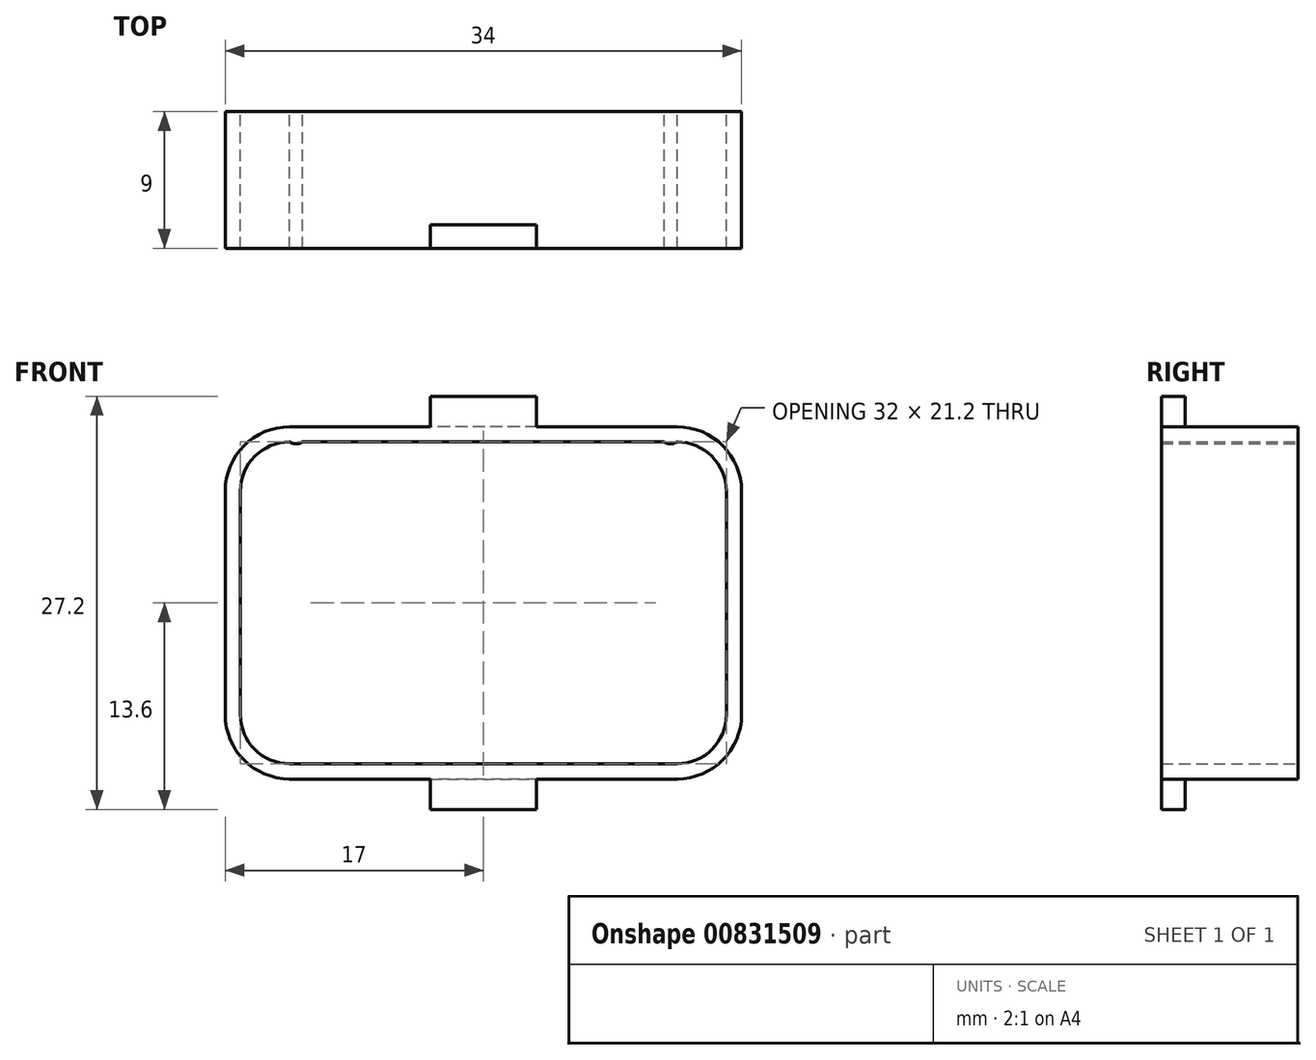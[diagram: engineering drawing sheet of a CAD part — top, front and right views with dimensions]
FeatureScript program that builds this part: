
annotation { "Feature Type Name" : "Feature", "Feature Type Description" : "" }
export const myFeature = defineFeature(function(context is Context, id is Id, definition is map)
    precondition{}
    {
        {
            var Q0;
            Q0=qCreatedBy(makeId("Front.planeOp"),FACE);
            var sketch = newSketch(context, id + "F0", { "sketchPlane" : qUnion([Q0])});
            skLineSegment(sketch, "E0.bottom", {"start": v(12.75, -10.6) * mm, "end": v(-12.75, -10.6) * mm});
            skLineSegment(sketch, "E0.top", {"start": v(12.75, 10.6) * mm, "end": v(-12.75, 10.6) * mm});
            skLineSegment(sketch, "E0.left", {"start": v(16, -7.35) * mm, "end": v(16, 7.35) * mm});
            skLineSegment(sketch, "E0.right", {"start": v(-16, -7.35) * mm, "end": v(-16, 7.35) * mm});
            skPoint(sketch, "E0.middle", {"position": v(0, 0) * mm});
            skPoint(sketch, "E1.visualSharp", {"position": v(-16, 10.6) * mm});
            skArc(sketch, "E1.filletArc", {"start": v(-12.75, 10.6) * mm, "mid": v(-15.05, 9.65) * mm, "end": v(-16, 7.35) * mm});
            skPoint(sketch, "E2.visualSharp", {"position": v(-16, -10.6) * mm});
            skArc(sketch, "E2.filletArc", {"start": v(-16, -7.35) * mm, "mid": v(-15.05, -9.65) * mm, "end": v(-12.75, -10.6) * mm});
            skPoint(sketch, "E3.visualSharp", {"position": v(16, -10.6) * mm});
            skArc(sketch, "E3.filletArc", {"start": v(12.75, -10.6) * mm, "mid": v(15.05, -9.65) * mm, "end": v(16, -7.35) * mm});
            skPoint(sketch, "E4.visualSharp", {"position": v(16, 10.6) * mm});
            skArc(sketch, "E4.filletArc", {"start": v(16, 7.35) * mm, "mid": v(15.05, 9.65) * mm, "end": v(12.75, 10.6) * mm});
            skArc(sketch, "E5.0", {"start": v(17, 7.35) * mm, "mid": v(15.76, 10.36) * mm, "end": v(12.75, 11.6) * mm});
            skLineSegment(sketch, "E5.1", {"start": v(17, -7.35) * mm, "end": v(17, 7.35) * mm});
            skLineSegment(sketch, "E5.2", {"start": v(12.75, 11.6) * mm, "end": v(-12.75, 11.6) * mm});
            skArc(sketch, "E5.3", {"start": v(12.75, -11.6) * mm, "mid": v(15.76, -10.36) * mm, "end": v(17, -7.35) * mm});
            skArc(sketch, "E5.4", {"start": v(-12.75, 11.6) * mm, "mid": v(-15.76, 10.36) * mm, "end": v(-17, 7.35) * mm});
            skLineSegment(sketch, "E5.5", {"start": v(-17, -7.35) * mm, "end": v(-17, 7.35) * mm});
            skArc(sketch, "E5.6", {"start": v(-17, -7.35) * mm, "mid": v(-15.76, -10.36) * mm, "end": v(-12.75, -11.6) * mm});
            skLineSegment(sketch, "E5.7", {"start": v(12.75, -11.6) * mm, "end": v(-12.75, -11.6) * mm});
            skSolve(sketch);
        }
        {
            var Q0;
            Q0=makeQuery(id+"F0.imprint","IMPRINT",FACE,{"disambiguationData":[TD([[makeQuery(id+"F0.imprint","IMPRINT",EDGE,{"derivedFrom":sQuery(id+"F0.wireOp",EDGE,"E0.bottom")}),1.0]])]});
            extrude(context, id + "F1", {"entities" : qUnion([Q0]), "depth" : 9 * mm, "offsetDistance" : 25 * mm});
        }
        {
            var Q0;
            Q0=makeQuery(id+"F1.opExtrude","SWEPT_FACE",FACE,{"disambiguationData":[OSD([sQuery(id+"F0.wireOp",EDGE,"E5.2")])]});
            var sketch = newSketch(context, id + "F2", { "sketchPlane" : qUnion([Q0])});
            skLineSegment(sketch, "E6.bottom", {"start": v(3.5, -7.44) * mm, "end": v(-3.5, -7.44) * mm});
            skLineSegment(sketch, "E6.top", {"start": v(3.5, -9) * mm, "end": v(-3.5, -9) * mm});
            skLineSegment(sketch, "E6.left", {"start": v(3.5, -7.44) * mm, "end": v(3.5, -9) * mm});
            skLineSegment(sketch, "E6.right", {"start": v(-3.5, -7.44) * mm, "end": v(-3.5, -9) * mm});
            skPoint(sketch, "E6.middle", {"position": v(0, -9) * mm});
            skLineSegment(sketch, "E7.MirrorCS", {"start": v(-3.5, -9) * mm, "end": v(3.5, -9) * mm});
            skLineSegment(sketch, "E8.MirrorCS", {"start": v(-3.5, -7.44) * mm, "end": v(3.5, -7.44) * mm});
            skSolve(sketch);
        }
        {
            var Q0;
            Q0=qSketchRegion(id+"F2",true);
            extrude(context, id + "F3", {"entities" : qUnion([Q0]), "operationType" : NewBodyOperationType.ADD, "depth" : 2 * mm, "offsetDistance" : 25 * mm});
        }
        {
            var Q0;
            Q0=qCreatedBy(makeId("Front.planeOp"),FACE);
            var sketch = newSketch(context, id + "F4", { "sketchPlane" : qUnion([Q0])});
            skArc(sketch, "E9", {"start": v(-12.75, 10.6) * mm, "mid": v(-12.33, 10.47) * mm, "end": v(-11.9, 10.6) * mm});
            skArc(sketch, "E10.MirrorCS", {"start": v(12.75, 10.6) * mm, "mid": v(12.33, 10.47) * mm, "end": v(11.9, 10.6) * mm});
            skLineSegment(sketch, "E11", {"start": v(-12.75, 10.6) * mm, "end": v(-11.9, 10.6) * mm});
            skLineSegment(sketch, "E12", {"start": v(11.9, 10.6) * mm, "end": v(12.75, 10.6) * mm});
            skSolve(sketch);
        }
        {
            var Q0;
            Q0=qSketchRegion(id+"F4",true);
            extrude(context, id + "F5", {"entities" : qUnion([Q0]), "operationType" : NewBodyOperationType.ADD, "depth" : 9 * mm, "offsetDistance" : 25 * mm});
        }
        {
            var Q0;
            Q0=qSketchRegion(id+"F4",true);
            extrude(context, id + "F6", {"entities" : qUnion([Q0]), "operationType" : NewBodyOperationType.ADD, "depth" : 9 * mm, "offsetDistance" : 25 * mm});
        }
        {
            var Q0;
            Q0=makeQuery(id+"F1.opExtrude","SWEPT_FACE",FACE,{"disambiguationData":[OSD([sQuery(id+"F0.wireOp",EDGE,"E5.7")])]});
            var sketch = newSketch(context, id + "F7", { "sketchPlane" : qUnion([Q0])});
            skLineSegment(sketch, "E13", {"start": v(0, 9) * mm, "end": v(-3.5, 9) * mm});
            skLineSegment(sketch, "E14", {"start": v(-3.5, 9) * mm, "end": v(-3.5, 7.44) * mm});
            skLineSegment(sketch, "E15", {"start": v(-3.5, 7.44) * mm, "end": v(0, 7.44) * mm});
            skLineSegment(sketch, "E16.MirrorCS", {"start": v(3.5, 9) * mm, "end": v(3.5, 7.44) * mm});
            skLineSegment(sketch, "E17.MirrorCS", {"start": v(3.5, 7.44) * mm, "end": v(0, 7.44) * mm});
            skLineSegment(sketch, "E18.MirrorCS", {"start": v(0, 9) * mm, "end": v(3.5, 9) * mm});
            skSolve(sketch);
        }
        {
            var Q0;
            Q0=makeQuery(id+"F7.imprint","IMPRINT",FACE,{"disambiguationData":[TD([[makeQuery(id+"F7.imprint","IMPRINT",EDGE,{"derivedFrom":sQuery(id+"F7.wireOp",EDGE,"E13")}),1.0]])]});
            extrude(context, id + "F8", {"entities" : qUnion([Q0]), "operationType" : NewBodyOperationType.ADD, "depth" : 2 * mm, "offsetDistance" : 25 * mm});
        }
    });
